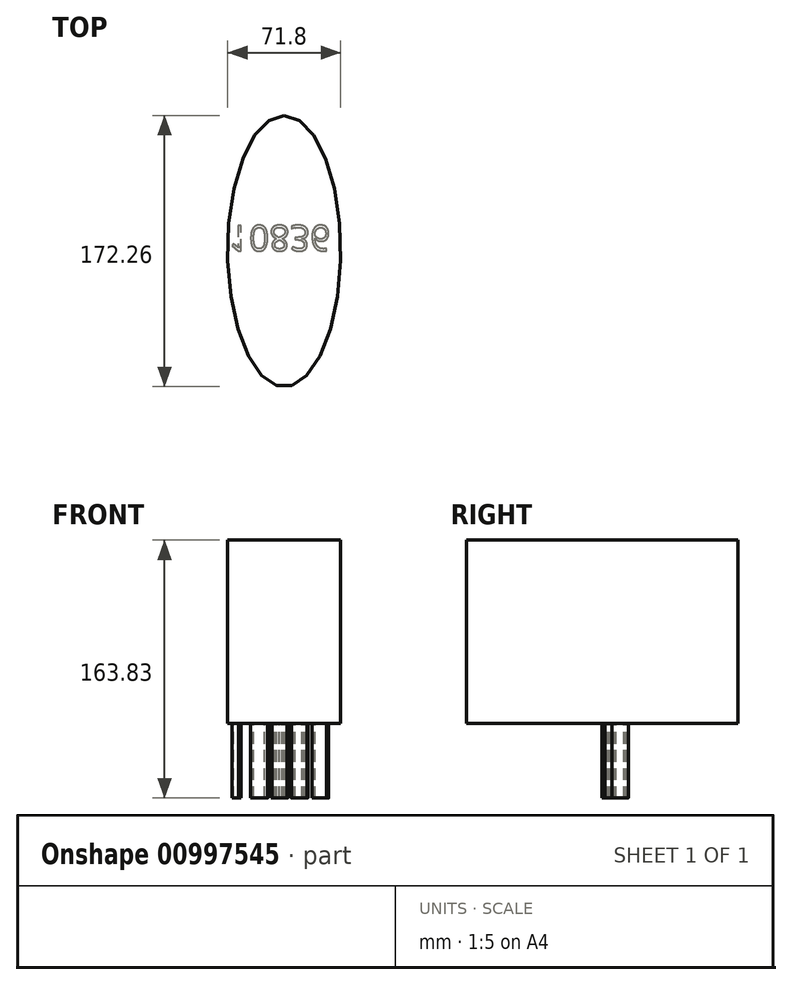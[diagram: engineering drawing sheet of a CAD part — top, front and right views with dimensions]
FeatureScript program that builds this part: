
annotation { "Feature Type Name" : "Feature", "Feature Type Description" : "" }
export const myFeature = defineFeature(function(context is Context, id is Id, definition is map)
    precondition{}
    {
        {
            var Q0;
            Q0=qCreatedBy(makeId("Top.planeOp"),FACE);
            var sketch = newSketch(context, id + "F0", { "sketchPlane" : qUnion([Q0])});
            skEllipse(sketch, "E0", {"center": v(0, 0) * mm, "majorRadius": 86.13 * mm, "minorRadius": 35.9 * mm, "majorAxis": v(0, 1)});
            skSolve(sketch);
        }
        {
            var Q0;
            Q0 = qSketchRegion(id + "F0", true);
            extrude(context, id + "F1", {"entities" : qUnion([Q0]), "oppositeDirection" : true, "depth" : 116.33 * mm, "offsetDistance" : 25.4 * mm});
        }
        {
            var Q0;
            Q0=makeQuery(id+"F1.opExtrude","CAP_FACE",FACE,{"disambiguationData":[OSD([sQuery(id+"F0.wireOp",EDGE,"E0")])],"isStart":false});
            var sketch = newSketch(context, id + "F2", { "sketchPlane" : qUnion([Q0])});
            skText(sketch, "E1", { "text": "10836\n", "fontName": "OpenSans-Regular.ttf"});
            const initialGuessF2  = {"E1": [-0.03525, -0.01628, 1, 0, 0.01628]};
            skSetInitialGuess(sketch, initialGuessF2);
            skSolve(sketch);
        }
        {
            var Q0;
            Q0 = qSketchRegion(id + "F2", true);
            extrude(context, id + "F3", {"entities" : qUnion([Q0]), "operationType" : NewBodyOperationType.ADD, "depth" : 47.5 * mm, "offsetDistance" : 25.4 * mm});
        }
    });
